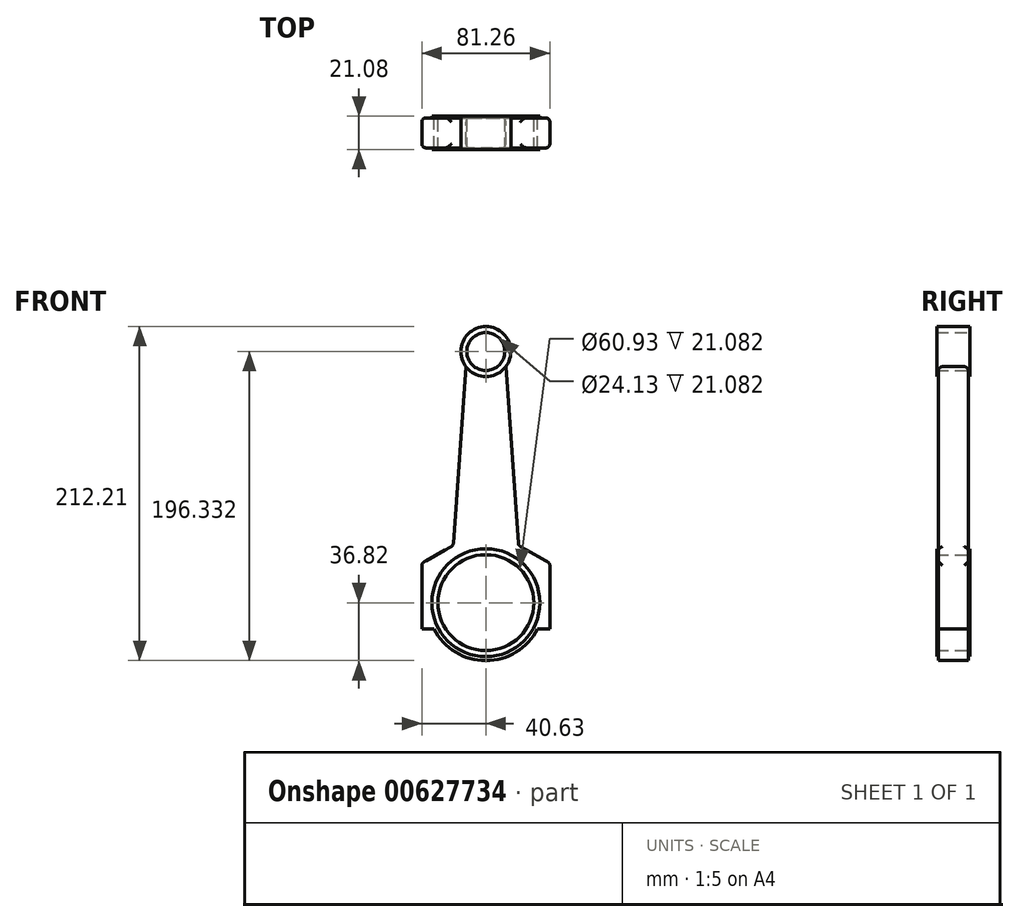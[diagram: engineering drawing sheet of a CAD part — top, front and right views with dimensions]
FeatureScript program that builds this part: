
annotation { "Feature Type Name" : "Feature", "Feature Type Description" : "" }
export const myFeature = defineFeature(function(context is Context, id is Id, definition is map)
    precondition{}
    {
        {
            var Q0;
            Q0=qCreatedBy(makeId("Front.planeOp"),FACE);
            var sketch = newSketch(context, id + "F0", { "sketchPlane" : qUnion([Q0])});
            skCircle(sketch, "E0", {"center": v(0, -90.39) * mm, "radius": 30.47 * mm});
            skLineSegment(sketch, "E1", {"start": v(0, -90.39) * mm, "end": v(0, 69.12) * mm, "construction": true});
            skCircle(sketch, "E2", {"center": v(0, 69.12) * mm, "radius": 12.07 * mm});
            skCircle(sketch, "E3.0", {"center": v(0, 69.12) * mm, "radius": 15.88 * mm});
            skLineSegment(sketch, "E4", {"start": v(0, -90.39) * mm, "end": v(-40.63, -90.39) * mm});
            skCircle(sketch, "E5.0", {"center": v(0, -90.39) * mm, "radius": 34.28 * mm});
            skArc(sketch, "E6.0", {"start": v(-32.87, -106.98) * mm, "mid": v(0, -127.2) * mm, "end": v(32.87, -106.98) * mm});
            skLineSegment(sketch, "E7", {"start": v(-40.63, -90.39) * mm, "end": v(-40.63, -65.24) * mm});
            skLineSegment(sketch, "E8", {"start": v(-40.63, -65.24) * mm, "end": v(-20.75, -54.1) * mm});
            skLineSegment(sketch, "E9", {"start": v(-20.75, -54.1) * mm, "end": v(-12.65, 59.54) * mm});
            skLineSegment(sketch, "E10.MirrorCS", {"start": v(20.75, -54.1) * mm, "end": v(12.65, 59.54) * mm});
            skLineSegment(sketch, "E11.MirrorCS", {"start": v(40.63, -65.24) * mm, "end": v(20.75, -54.1) * mm});
            skLineSegment(sketch, "E12.MirrorCS", {"start": v(40.63, -90.39) * mm, "end": v(40.63, -65.24) * mm});
            skLineSegment(sketch, "E13.MirrorCS", {"start": v(0, -90.39) * mm, "end": v(40.63, -90.39) * mm});
            skLineSegment(sketch, "E14", {"start": v(-40.63, -90.39) * mm, "end": v(-40.63, -106.98) * mm});
            skLineSegment(sketch, "E15", {"start": v(-40.63, -106.98) * mm, "end": v(-32.87, -106.98) * mm});
            skLineSegment(sketch, "E16.MirrorCS", {"start": v(40.63, -106.98) * mm, "end": v(32.87, -106.98) * mm});
            skLineSegment(sketch, "E17.MirrorCS", {"start": v(40.63, -90.39) * mm, "end": v(40.63, -106.98) * mm});
            skPoint(sketch, "E18.orphan", {"position": v(-12.03, 68.25) * mm});
            skPoint(sketch, "E19.orphan", {"position": v(12.03, 68.25) * mm});
            skSolve(sketch);
        }
        {
            var Q0;
            {var subQ0=sQuery(id+"F0.wireOp",EDGE,"E4");var subQ1=sQuery(id+"F0.wireOp",EDGE,"E0");var subQ2=makeQuery(id+"F0.imprint","INTERSECT",VERTEX,{"derivedFrom":[subQ1,subQ0]});Q0=makeQuery(id+"F0.imprint","IMPRINT",FACE,{"disambiguationData":[TD([[makeQuery(id+"F0.imprint","IMPRINT",EDGE,{"disambiguationData":[TD([[subQ2,1.0]])],"derivedFrom":subQ1}),-1.0]])]});}
            extrude(context, id + "F1", {"entities" : qUnion([Q0]), "endBound" : BoundingType.SYMMETRIC, "depth" : 21.08 * mm, "offsetDistance" : 25.4 * mm});
        }
        {
            var Q0;
            {var subQ0=sQuery(id+"F0.wireOp",EDGE,"E7");Q0=makeQuery(id+"F0.imprint","IMPRINT",FACE,{"disambiguationData":[TD([[makeQuery(id+"F0.imprint","IMPRINT",EDGE,{"derivedFrom":subQ0}),-1.0]])]});}
            extrude(context, id + "F2", {"entities" : qUnion([Q0]), "operationType" : NewBodyOperationType.ADD, "endBound" : BoundingType.SYMMETRIC, "depth" : 19.05 * mm, "offsetDistance" : 25.4 * mm});
        }
        {
            var Q0;
            {var subQ0=sQuery(id+"F0.wireOp",EDGE,"E4");var subQ1=sQuery(id+"F0.wireOp",EDGE,"E0");var subQ2=makeQuery(id+"F0.imprint","INTERSECT",VERTEX,{"derivedFrom":[subQ1,subQ0]});Q0=makeQuery(id+"F0.imprint","IMPRINT",FACE,{"disambiguationData":[TD([[makeQuery(id+"F0.imprint","IMPRINT",EDGE,{"disambiguationData":[TD([[subQ2,-1.0]])],"derivedFrom":subQ1}),-1.0]])]});}
            extrude(context, id + "F3", {"entities" : qUnion([Q0]), "endBound" : BoundingType.SYMMETRIC, "depth" : 21.08 * mm, "offsetDistance" : 25.4 * mm});
        }
        {
            var Q0;
            Q0=makeQuery(id+"F0.imprint","IMPRINT",FACE,{"disambiguationData":[TD([[makeQuery(id+"F0.imprint","IMPRINT",EDGE,{"derivedFrom":sQuery(id+"F0.wireOp",EDGE,"E6.0")}),1.0]])]});
            extrude(context, id + "F4", {"entities" : qUnion([Q0]), "operationType" : NewBodyOperationType.ADD, "endBound" : BoundingType.SYMMETRIC, "depth" : 19.05 * mm, "offsetDistance" : 25.4 * mm});
        }
        {
            var Q0;
            Q0=makeQuery(id+"F0.imprint","IMPRINT",FACE,{"disambiguationData":[TD([[makeQuery(id+"F0.imprint","IMPRINT",EDGE,{"derivedFrom":sQuery(id+"F0.wireOp",EDGE,"E2")}),-1.0]])]});
            extrude(context, id + "F5", {"entities" : qUnion([Q0]), "operationType" : NewBodyOperationType.ADD, "endBound" : BoundingType.SYMMETRIC, "depth" : 21.08 * mm, "offsetDistance" : 25.4 * mm});
        }
        {
            var Q0;
            Q0=makeQuery(id+"F2.opExtrude","CAP_EDGE",EDGE,{"disambiguationData":[OSD([sQuery(id+"F0.wireOp",EDGE,"E10.MirrorCS")])],"isStart":true});
            var Q1;
            Q1=makeQuery(id+"F2.opExtrude","CAP_EDGE",EDGE,{"disambiguationData":[OSD([sQuery(id+"F0.wireOp",EDGE,"E9")])],"isStart":true});
            var Q2;
            Q2=makeQuery(id+"F2.opExtrude","CAP_EDGE",EDGE,{"disambiguationData":[OSD([sQuery(id+"F0.wireOp",EDGE,"E9")])],"isStart":false});
            var Q3;
            Q3=makeQuery(id+"F2.opExtrude","CAP_EDGE",EDGE,{"disambiguationData":[OSD([sQuery(id+"F0.wireOp",EDGE,"E10.MirrorCS")])],"isStart":false});
            var Q4;
            Q4=makeQuery(id+"F2.opExtrude","SWEPT_EDGE",EDGE,{"disambiguationData":[OSD([sQuery(id+"F0.wireOp",EDGE,"E10.MirrorCS"),sQuery(id+"F0.wireOp",EDGE,"E11.MirrorCS")])]});
            var Q5;
            Q5=makeQuery(id+"F2.opExtrude","SWEPT_EDGE",EDGE,{"disambiguationData":[OSD([sQuery(id+"F0.wireOp",EDGE,"E8"),sQuery(id+"F0.wireOp",EDGE,"E9")])]});
            var Q6;
            Q6=makeQuery(id+"F2.opExtrude","CAP_EDGE",EDGE,{"disambiguationData":[OSD([sQuery(id+"F0.wireOp",EDGE,"E7")])],"isStart":false});
            var Q7;
            Q7=makeQuery(id+"F2.opExtrude","CAP_EDGE",EDGE,{"disambiguationData":[OSD([sQuery(id+"F0.wireOp",EDGE,"E7")])],"isStart":true});
            var Q8;
            Q8=makeQuery(id+"F2.opExtrude","SWEPT_EDGE",EDGE,{"disambiguationData":[OSD([sQuery(id+"F0.wireOp",EDGE,"E7"),sQuery(id+"F0.wireOp",EDGE,"E8")])]});
            var Q9;
            Q9=makeQuery(id+"F4.opExtrude","CAP_EDGE",EDGE,{"disambiguationData":[OSD([sQuery(id+"F0.wireOp",EDGE,"E14")])],"isStart":false});
            var Q10;
            Q10=makeQuery(id+"F4.opExtrude","CAP_EDGE",EDGE,{"disambiguationData":[OSD([sQuery(id+"F0.wireOp",EDGE,"E14")])],"isStart":true});
            var Q11;
            Q11=makeQuery(id+"F2.opExtrude","SWEPT_EDGE",EDGE,{"disambiguationData":[OSD([sQuery(id+"F0.wireOp",EDGE,"E11.MirrorCS"),sQuery(id+"F0.wireOp",EDGE,"E12.MirrorCS")])]});
            var Q12;
            Q12=makeQuery(id+"F2.opExtrude","CAP_EDGE",EDGE,{"disambiguationData":[OSD([sQuery(id+"F0.wireOp",EDGE,"E12.MirrorCS")])],"isStart":false});
            var Q13;
            Q13=makeQuery(id+"F4.opExtrude","CAP_EDGE",EDGE,{"disambiguationData":[OSD([sQuery(id+"F0.wireOp",EDGE,"E17.MirrorCS")])],"isStart":false});
            var Q14;
            Q14=makeQuery(id+"F2.opExtrude","CAP_EDGE",EDGE,{"disambiguationData":[OSD([sQuery(id+"F0.wireOp",EDGE,"E12.MirrorCS")])],"isStart":true});
            var Q15;
            Q15=makeQuery(id+"F4.opExtrude","CAP_EDGE",EDGE,{"disambiguationData":[OSD([sQuery(id+"F0.wireOp",EDGE,"E17.MirrorCS")])],"isStart":true});
            fillet(context, id + "F6", {"entities" : qUnion([Q0, Q1, Q2, Q3, Q4, Q5, Q6, Q7, Q8, Q9, Q10, Q11, Q12, Q13, Q14, Q15]), "radius" : 2.54 * mm, "tangentPropagation" : true, "allowEdgeOverflow" : false});
        }
    });
